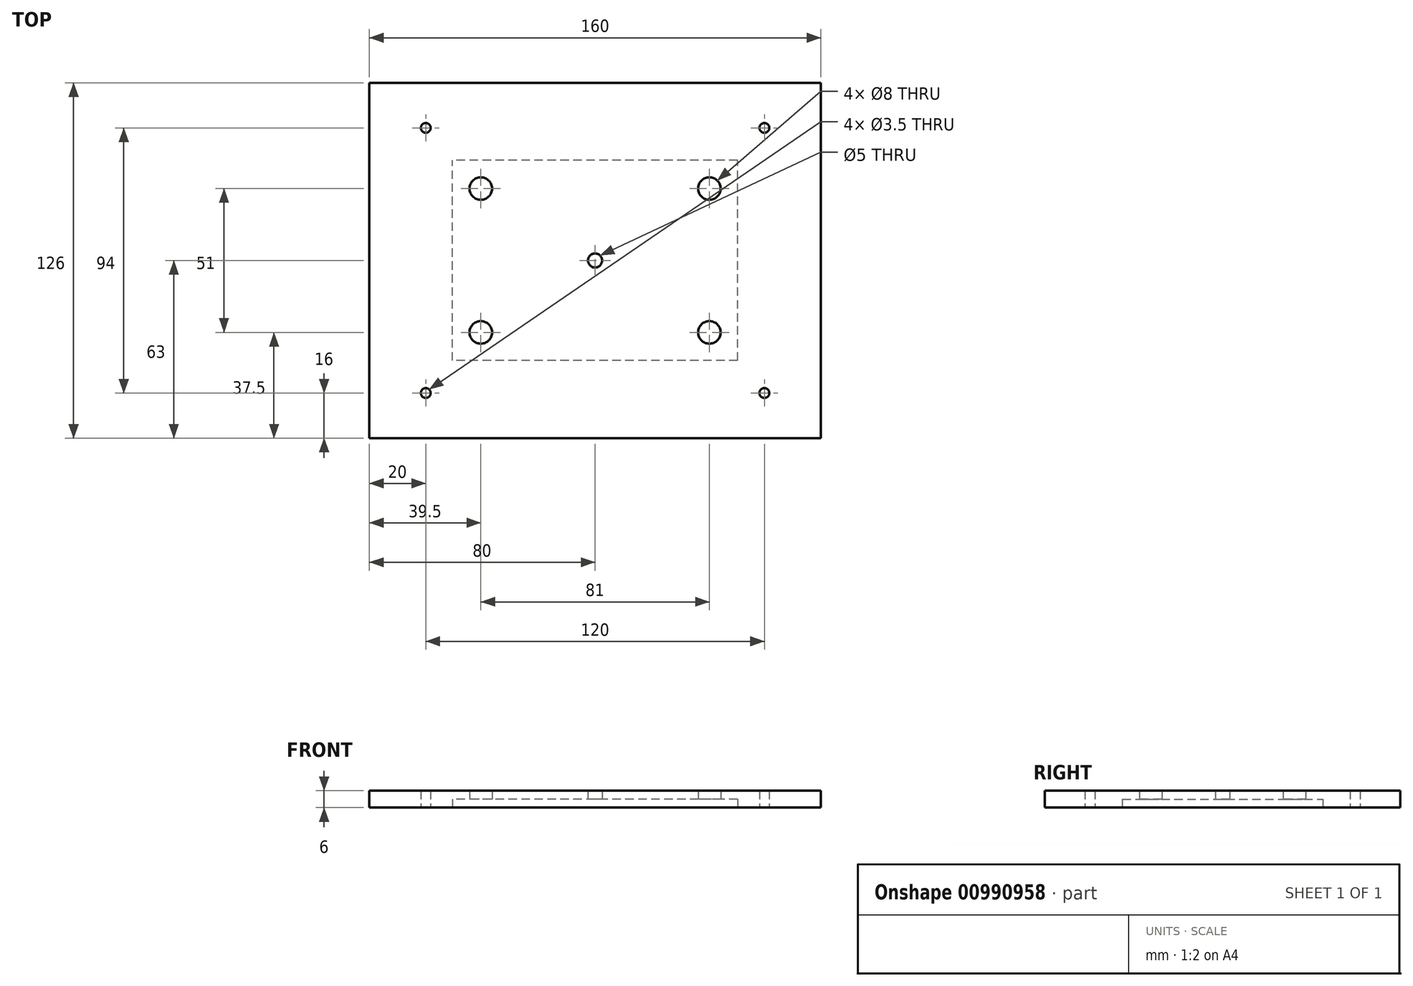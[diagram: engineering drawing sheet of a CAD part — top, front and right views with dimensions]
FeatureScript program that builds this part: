
annotation { "Feature Type Name" : "Feature", "Feature Type Description" : "" }
export const myFeature = defineFeature(function(context is Context, id is Id, definition is map)
    precondition{}
    {
        {
            var Q0;
            Q0=qCreatedBy(makeId("Top.planeOp"),FACE);
            var sketch = newSketch(context, id + "F0", { "sketchPlane" : qUnion([Q0])});
            skLineSegment(sketch, "E0.bottom", {"start": v(80, -63) * mm, "end": v(-80, -63) * mm});
            skLineSegment(sketch, "E0.top", {"start": v(80, 63) * mm, "end": v(-80, 63) * mm});
            skLineSegment(sketch, "E0.left", {"start": v(80, -63) * mm, "end": v(80, 63) * mm});
            skLineSegment(sketch, "E0.right", {"start": v(-80, -63) * mm, "end": v(-80, 63) * mm});
            skPoint(sketch, "E0.middle", {"position": v(0, 0) * mm});
            skLineSegment(sketch, "E1.bottom", {"start": v(60, -47) * mm, "end": v(-60, -47) * mm, "construction": true});
            skLineSegment(sketch, "E1.top", {"start": v(60, 47) * mm, "end": v(-60, 47) * mm, "construction": true});
            skLineSegment(sketch, "E1.left", {"start": v(60, -47) * mm, "end": v(60, 47) * mm, "construction": true});
            skLineSegment(sketch, "E1.right", {"start": v(-60, -47) * mm, "end": v(-60, 47) * mm, "construction": true});
            skCircle(sketch, "E2", {"center": v(-60, 47) * mm, "radius": 1.75 * mm});
            skCircle(sketch, "E3.MirrorC", {"center": v(60, 47) * mm, "radius": 1.75 * mm});
            skCircle(sketch, "E4.MirrorC", {"center": v(-60, -47) * mm, "radius": 1.75 * mm});
            skCircle(sketch, "E5.MirrorC", {"center": v(60, -47) * mm, "radius": 1.75 * mm});
            skLineSegment(sketch, "E6.bottom", {"start": v(50.5, -35.5) * mm, "end": v(-50.5, -35.5) * mm});
            skLineSegment(sketch, "E6.top", {"start": v(50.5, 35.5) * mm, "end": v(-50.5, 35.5) * mm});
            skLineSegment(sketch, "E6.left", {"start": v(50.5, -35.5) * mm, "end": v(50.5, 35.5) * mm});
            skLineSegment(sketch, "E6.right", {"start": v(-50.5, -35.5) * mm, "end": v(-50.5, 35.5) * mm});
            skLineSegment(sketch, "E7.bottom", {"start": v(40.5, -25.5) * mm, "end": v(-40.5, -25.5) * mm, "construction": true});
            skLineSegment(sketch, "E7.top", {"start": v(40.5, 25.5) * mm, "end": v(-40.5, 25.5) * mm, "construction": true});
            skLineSegment(sketch, "E7.left", {"start": v(40.5, -25.5) * mm, "end": v(40.5, 25.5) * mm, "construction": true});
            skLineSegment(sketch, "E7.right", {"start": v(-40.5, -25.5) * mm, "end": v(-40.5, 25.5) * mm, "construction": true});
            skCircle(sketch, "E8", {"center": v(-40.5, 25.5) * mm, "radius": 4 * mm});
            skCircle(sketch, "E9.MirrorC", {"center": v(40.5, 25.5) * mm, "radius": 4 * mm});
            skCircle(sketch, "E10.MirrorC", {"center": v(-40.5, -25.5) * mm, "radius": 4 * mm});
            skCircle(sketch, "E11.MirrorC", {"center": v(40.5, -25.5) * mm, "radius": 4 * mm});
            skCircle(sketch, "E12", {"center": v(0, 0) * mm, "radius": 2.5 * mm});
            skSolve(sketch);
        }
        {
            var Q0;
            Q0=makeQuery(id+"F0.imprint","IMPRINT",FACE,{"disambiguationData":[TD([[makeQuery(id+"F0.imprint","IMPRINT",EDGE,{"derivedFrom":sQuery(id+"F0.wireOp",EDGE,"E0.bottom")}),-1.0]])]});
            var Q1;
            Q1=makeQuery(id+"F0.imprint","IMPRINT",FACE,{"disambiguationData":[TD([[makeQuery(id+"F0.imprint","IMPRINT",EDGE,{"derivedFrom":sQuery(id+"F0.wireOp",EDGE,"E6.bottom")}),-1.0]])]});
            extrude(context, id + "F1", {"entities" : qUnion([Q0, Q1]), "depth" : 6 * mm, "offsetDistance" : 25 * mm});
        }
        {
            var Q0;
            Q0=makeQuery(id+"F0.imprint","IMPRINT",FACE,{"disambiguationData":[TD([[makeQuery(id+"F0.imprint","IMPRINT",EDGE,{"derivedFrom":sQuery(id+"F0.wireOp",EDGE,"E6.bottom")}),-1.0]])]});
            extrude(context, id + "F2", {"entities" : qUnion([Q0]), "operationType" : NewBodyOperationType.REMOVE, "depth" : 3 * mm, "offsetDistance" : 25 * mm});
        }
    });
